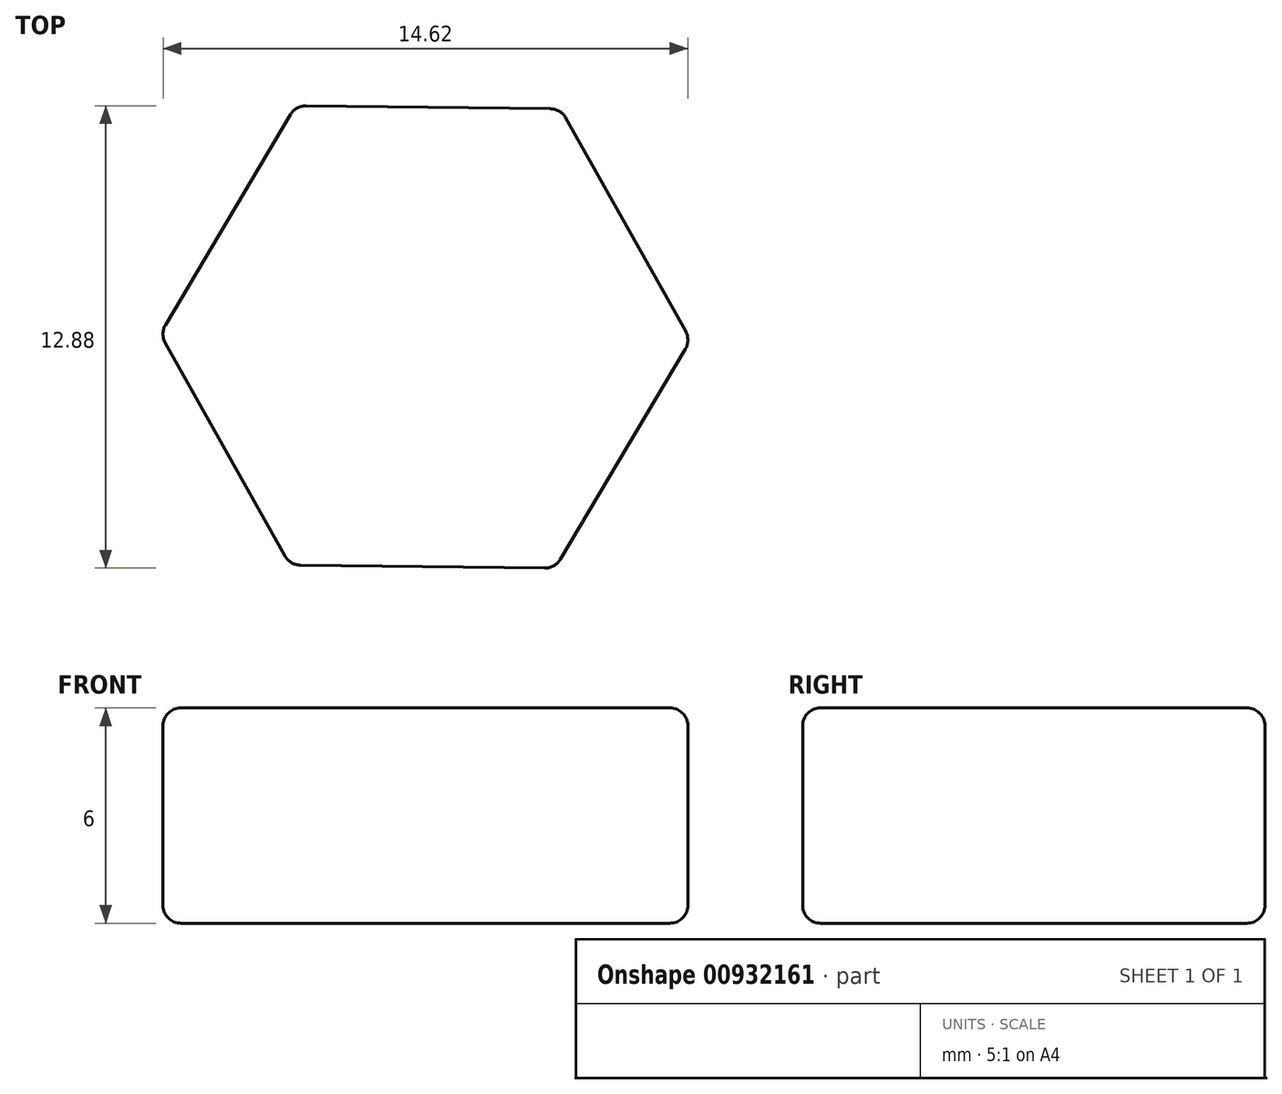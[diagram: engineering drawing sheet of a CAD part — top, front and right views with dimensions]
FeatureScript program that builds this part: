
annotation { "Feature Type Name" : "Feature", "Feature Type Description" : "" }
export const myFeature = defineFeature(function(context is Context, id is Id, definition is map)
    precondition{}
    {
        {
            var Q0;
            Q0=qCreatedBy(makeId("Top.planeOp"),FACE);
            var sketch = newSketch(context, id + "F0", { "sketchPlane" : qUnion([Q0])});
            skCircle(sketch, "E0.cCircle", {"center": v(-17.11, 11.09) * mm, "radius": 6.4 * mm, "construction": true});
            skLineSegment(sketch, "E0.0", {"start": v(-13.34, 17.44) * mm, "end": v(-9.72, 11) * mm});
            skLineSegment(sketch, "E0.1", {"start": v(-9.72, 11) * mm, "end": v(-13.5, 4.64) * mm});
            skLineSegment(sketch, "E0.2", {"start": v(-13.5, 4.64) * mm, "end": v(-20.88, 4.73) * mm});
            skLineSegment(sketch, "E0.3", {"start": v(-20.88, 4.73) * mm, "end": v(-24.5, 11.18) * mm});
            skLineSegment(sketch, "E0.4", {"start": v(-24.5, 11.18) * mm, "end": v(-20.73, 17.53) * mm});
            skLineSegment(sketch, "E0.5", {"start": v(-20.73, 17.53) * mm, "end": v(-13.34, 17.44) * mm});
            skPoint(sketch, "E0.0.midPoint", {"position": v(-11.53, 14.22) * mm});
            skSolve(sketch);
        }
        {
            var Q0;
            Q0=qSketchRegion(id+"F0",true);
            extrude(context, id + "F1", {"entities" : qUnion([Q0]), "depth" : 6 * mm, "offsetDistance" : 25 * mm});
        }
        {
            var Q0;
            Q0=makeQuery(id+"F1.opExtrude","CAP_FACE",FACE,{"disambiguationData":[OSD([sQuery(id+"F0.wireOp",EDGE,"E0.0"),sQuery(id+"F0.wireOp",EDGE,"E0.1"),sQuery(id+"F0.wireOp",EDGE,"E0.2"),sQuery(id+"F0.wireOp",EDGE,"E0.3"),sQuery(id+"F0.wireOp",EDGE,"E0.4"),sQuery(id+"F0.wireOp",EDGE,"E0.5")])],"isStart":false});
            var Q1;
            Q1=makeQuery(id+"F1.opExtrude","CAP_FACE",FACE,{"disambiguationData":[OSD([sQuery(id+"F0.wireOp",EDGE,"E0.0"),sQuery(id+"F0.wireOp",EDGE,"E0.1"),sQuery(id+"F0.wireOp",EDGE,"E0.2"),sQuery(id+"F0.wireOp",EDGE,"E0.3"),sQuery(id+"F0.wireOp",EDGE,"E0.4"),sQuery(id+"F0.wireOp",EDGE,"E0.5")])],"isStart":true});
            var Q2;
            Q2=makeQuery(id+"F1.opExtrude","SWEPT_FACE",FACE,{"disambiguationData":[OSD([sQuery(id+"F0.wireOp",EDGE,"E0.2")])]});
            var Q3;
            Q3=makeQuery(id+"F1.opExtrude","SWEPT_FACE",FACE,{"disambiguationData":[OSD([sQuery(id+"F0.wireOp",EDGE,"E0.1")])]});
            var Q4;
            Q4=makeQuery(id+"F1.opExtrude","SWEPT_FACE",FACE,{"disambiguationData":[OSD([sQuery(id+"F0.wireOp",EDGE,"E0.3")])]});
            var Q5;
            Q5=makeQuery(id+"F1.opExtrude","SWEPT_FACE",FACE,{"disambiguationData":[OSD([sQuery(id+"F0.wireOp",EDGE,"E0.4")])]});
            var Q6;
            Q6=makeQuery(id+"F1.opExtrude","SWEPT_FACE",FACE,{"disambiguationData":[OSD([sQuery(id+"F0.wireOp",EDGE,"E0.5")])]});
            fillet(context, id + "F2", {"entities" : qUnion([Q0, Q1, Q2, Q3, Q4, Q5, Q6]), "radius" : 0.5 * mm, "tangentPropagation" : true, "allowEdgeOverflow" : false});
        }
    });
